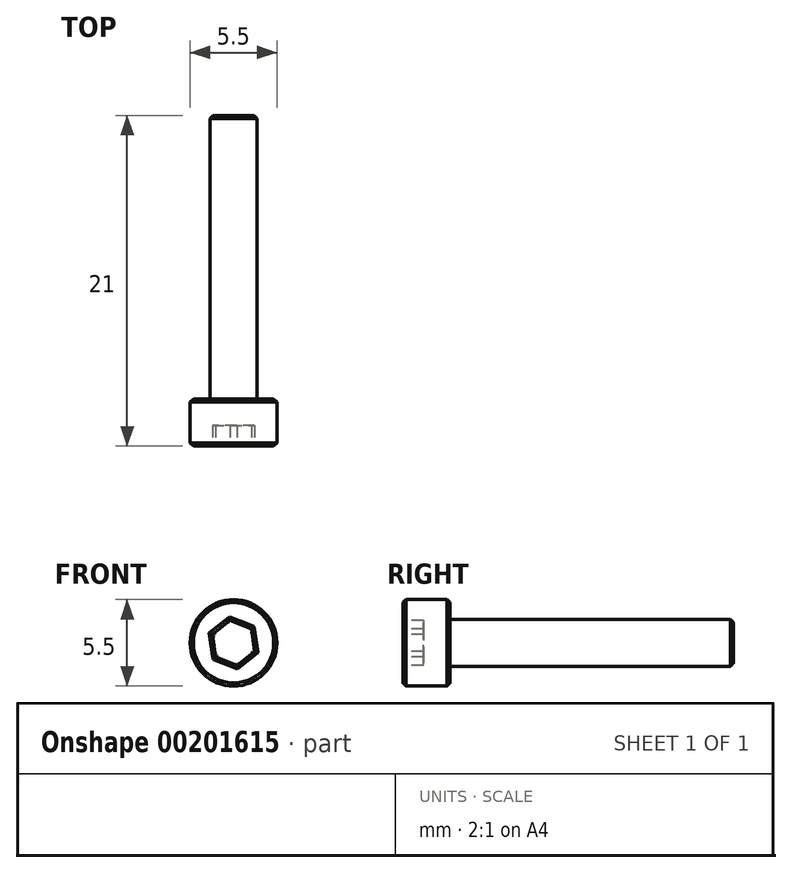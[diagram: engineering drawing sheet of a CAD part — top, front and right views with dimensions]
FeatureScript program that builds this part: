
annotation { "Feature Type Name" : "Feature", "Feature Type Description" : "" }
export const myFeature = defineFeature(function(context is Context, id is Id, definition is map)
    precondition{}
    {
        {
            var Q0;
            Q0=qCreatedBy(makeId("Front.planeOp"),FACE);
            var sketch = newSketch(context, id + "F0", { "sketchPlane" : qUnion([Q0])});
            skCircle(sketch, "E0", {"center": v(0, 0) * mm, "radius": 1.5 * mm});
            skSolve(sketch);
        }
        {
            var Q0;
            Q0=makeQuery(id+"F0.imprint","IMPRINT",FACE,{"disambiguationData":[TD([[makeQuery(id+"F0.imprint","IMPRINT",EDGE,{"derivedFrom":sQuery(id+"F0.wireOp",EDGE,"E0")}),1.0]])]});
            extrude(context, id + "F1", {"entities" : qUnion([Q0]), "depth" : 18 * mm});
        }
        {
            var Q0;
            Q0=makeQuery(id+"F1.opExtrude","CAP_FACE",FACE,{"disambiguationData":[OSD([sQuery(id+"F0.wireOp",EDGE,"E0")])],"isStart":false});
            var sketch = newSketch(context, id + "F2", { "sketchPlane" : qUnion([Q0])});
            skCircle(sketch, "E1", {"center": v(0, 0) * mm, "radius": 2.75 * mm});
            skSolve(sketch);
        }
        {
            var Q0;
            Q0=qSketchRegion(id+"F2",true);
            extrude(context, id + "F3", {"entities" : qUnion([Q0]), "operationType" : NewBodyOperationType.ADD, "depth" : 3 * mm});
        }
        {
            var Q0;
            Q0=makeQuery(id+"F3.opExtrude","CAP_FACE",FACE,{"disambiguationData":[OSD([sQuery(id+"F2.wireOp",EDGE,"E1")])],"isStart":false});
            var sketch = newSketch(context, id + "F4", { "sketchPlane" : qUnion([Q0])});
            skCircle(sketch, "E2.cCircle", {"center": v(0, 0) * mm, "radius": 1.25 * mm, "construction": true});
            skLineSegment(sketch, "E2.0", {"start": v(1.34, -0.53) * mm, "end": v(0.21, -1.43) * mm});
            skLineSegment(sketch, "E2.1", {"start": v(0.21, -1.43) * mm, "end": v(-1.13, -0.9) * mm});
            skLineSegment(sketch, "E2.2", {"start": v(-1.13, -0.9) * mm, "end": v(-1.34, 0.53) * mm});
            skLineSegment(sketch, "E2.3", {"start": v(-1.34, 0.53) * mm, "end": v(-0.21, 1.43) * mm});
            skLineSegment(sketch, "E2.4", {"start": v(-0.21, 1.43) * mm, "end": v(1.13, 0.9) * mm});
            skLineSegment(sketch, "E2.5", {"start": v(1.13, 0.9) * mm, "end": v(1.34, -0.53) * mm});
            skPoint(sketch, "E2.0.midPoint", {"position": v(0.78, -0.98) * mm});
            skSolve(sketch);
        }
        {
            var Q0;
            Q0=makeQuery(id+"F4.imprint","IMPRINT",FACE,{"disambiguationData":[TD([[makeQuery(id+"F4.imprint","IMPRINT",EDGE,{"derivedFrom":sQuery(id+"F4.wireOp",EDGE,"E2.0")}),-1.0]])]});
            extrude(context, id + "F5", {"entities" : qUnion([Q0]), "operationType" : NewBodyOperationType.REMOVE, "oppositeDirection" : true, "depth" : 1.3 * mm});
        }
        {
            var Q0;
            Q0=makeQuery(id+"F3.opExtrude","CAP_EDGE",EDGE,{"disambiguationData":[OSD([sQuery(id+"F2.wireOp",EDGE,"E1")])],"isStart":false});
            var Q1;
            Q1=makeQuery(id+"F3.opExtrude","CAP_EDGE",EDGE,{"disambiguationData":[OSD([sQuery(id+"F2.wireOp",EDGE,"E1")])],"isStart":true});
            var Q2;
            Q2=makeQuery(id+"F1.opExtrude","CAP_EDGE",EDGE,{"disambiguationData":[OSD([sQuery(id+"F0.wireOp",EDGE,"E0")])],"isStart":true});
            var Q3;
            Q3=makeQuery(id+"F3.opExtrude","CAP_FACE",FACE,{"disambiguationData":[OSD([sQuery(id+"F2.wireOp",EDGE,"E1")])],"isStart":false});
            chamfer(context, id + "F6", {"entities" : qUnion([Q0, Q1, Q2, Q3]), "width" : .2 * mm, "tangentPropagation" : true});
        }
    });
